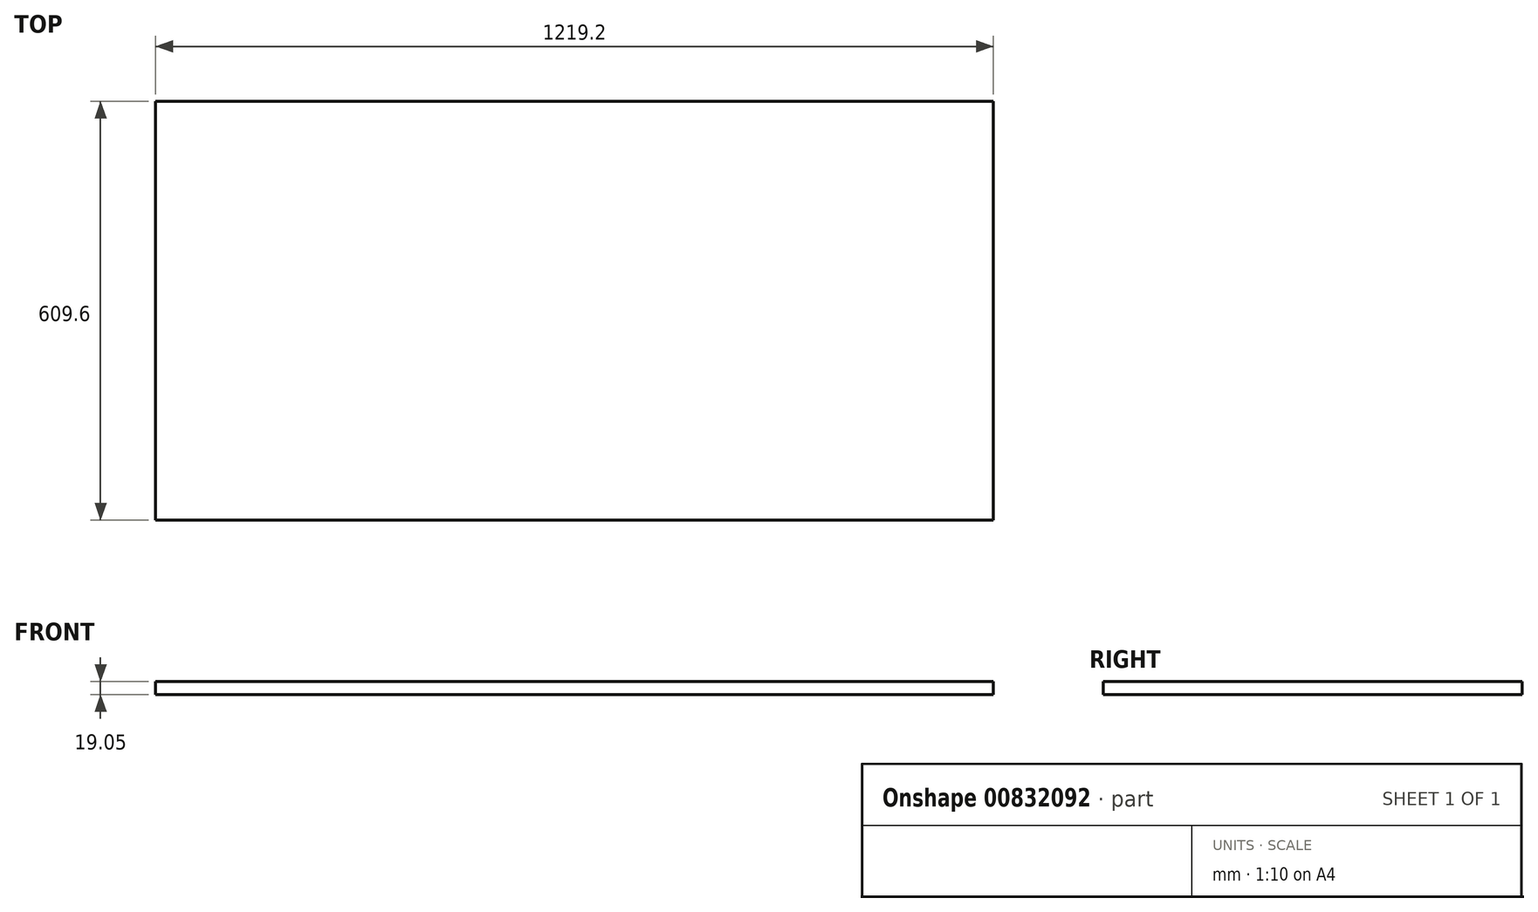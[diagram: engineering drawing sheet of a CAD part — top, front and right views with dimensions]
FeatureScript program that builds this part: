
annotation { "Feature Type Name" : "Feature", "Feature Type Description" : "" }
export const myFeature = defineFeature(function(context is Context, id is Id, definition is map)
    precondition{}
    {
        {
            var Q0;
            Q0=qCreatedBy(makeId("Top.planeOp"),FACE);
            var sketch = newSketch(context, id + "F0", { "sketchPlane" : qUnion([Q0])});
            skLineSegment(sketch, "E0.bottom", {"start": v(0, 0) * mm, "end": v(1219.2, 0) * mm});
            skLineSegment(sketch, "E0.top", {"start": v(0, 609.6) * mm, "end": v(1219.2, 609.6) * mm});
            skLineSegment(sketch, "E0.left", {"start": v(0, 0) * mm, "end": v(0, 609.6) * mm});
            skLineSegment(sketch, "E0.right", {"start": v(1219.2, 0) * mm, "end": v(1219.2, 609.6) * mm});
            skSolve(sketch);
        }
        {
            var Q0;
            Q0=makeQuery(id+"F0.imprint","IMPRINT",FACE,{"disambiguationData":[TD([[makeQuery(id+"F0.imprint","IMPRINT",EDGE,{"derivedFrom":sQuery(id+"F0.wireOp",EDGE,"E0.bottom")}),1.0]])]});
            extrude(context, id + "F1", {"entities" : qUnion([Q0]), "depth" : 19.05 * mm, "offsetDistance" : 25.4 * mm});
        }
    });
